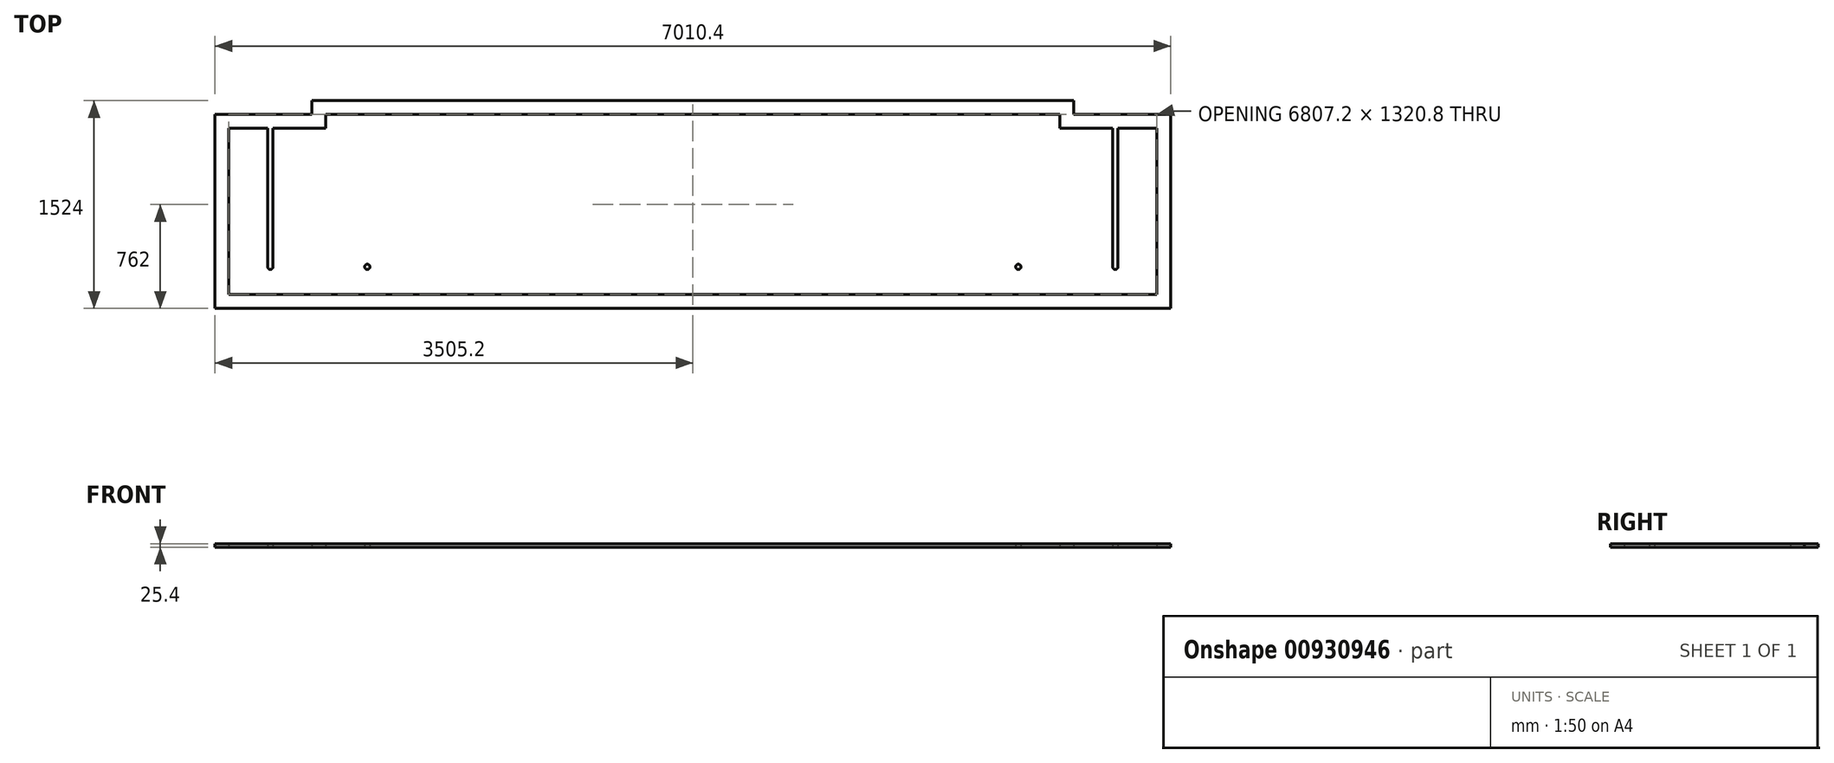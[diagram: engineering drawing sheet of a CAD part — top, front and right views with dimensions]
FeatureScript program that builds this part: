
annotation { "Feature Type Name" : "Feature", "Feature Type Description" : "" }
export const myFeature = defineFeature(function(context is Context, id is Id, definition is map)
    precondition{}
    {
        {
            var Q0;
            Q0=qCreatedBy(makeId("Top.planeOp"),FACE);
            var sketch = newSketch(context, id + "F0", { "sketchPlane" : qUnion([Q0])});
            skLineSegment(sketch, "E0.top", {"start": v(0, -1422.4) * mm, "end": v(7010.4, -1422.4) * mm});
            skLineSegment(sketch, "E0.left", {"start": v(0, 0) * mm, "end": v(0, -1422.4) * mm});
            skLineSegment(sketch, "E0.right", {"start": v(7010.4, 0) * mm, "end": v(7010.4, -1422.4) * mm});
            skLineSegment(sketch, "E1.top", {"start": v(101.6, -1320.8) * mm, "end": v(6908.8, -1320.8) * mm});
            skLineSegment(sketch, "E1.left", {"start": v(101.6, -101.6) * mm, "end": v(101.6, -1320.8) * mm});
            skLineSegment(sketch, "E1.right", {"start": v(6908.8, -101.6) * mm, "end": v(6908.8, -1320.8) * mm});
            skLineSegment(sketch, "E2.bottom", {"start": v(387.35, -101.6) * mm, "end": v(425.45, -101.6) * mm});
            skLineSegment(sketch, "E2.top", {"start": v(387.35, -1117.6) * mm, "end": v(425.45, -1117.6) * mm});
            skLineSegment(sketch, "E2.left", {"start": v(387.35, -101.6) * mm, "end": v(387.35, -1117.6) * mm});
            skLineSegment(sketch, "E2.right", {"start": v(425.45, -101.6) * mm, "end": v(425.45, -1117.6) * mm});
            skLineSegment(sketch, "E3.bottom", {"start": v(6584.95, -101.6) * mm, "end": v(6623.05, -101.6) * mm});
            skLineSegment(sketch, "E3.top", {"start": v(6584.95, -1117.6) * mm, "end": v(6623.05, -1117.6) * mm});
            skLineSegment(sketch, "E3.left", {"start": v(6584.95, -101.6) * mm, "end": v(6584.95, -1117.6) * mm});
            skLineSegment(sketch, "E3.right", {"start": v(6623.05, -101.6) * mm, "end": v(6623.05, -1117.6) * mm});
            skCircle(sketch, "E4", {"center": v(406.4, -1117.6) * mm, "radius": 19.05 * mm});
            skCircle(sketch, "E5", {"center": v(6604, -1117.6) * mm, "radius": 19.05 * mm});
            skLineSegment(sketch, "E6", {"start": v(101.6, -101.6) * mm, "end": v(812.8, -101.6) * mm});
            skLineSegment(sketch, "E7", {"start": v(812.8, -101.6) * mm, "end": v(812.8, 0) * mm});
            skLineSegment(sketch, "E8", {"start": v(812.8, 0) * mm, "end": v(6197.6, 0) * mm});
            skLineSegment(sketch, "E9", {"start": v(6197.6, 0) * mm, "end": v(6197.6, -101.6) * mm});
            skLineSegment(sketch, "E10", {"start": v(6197.6, -101.6) * mm, "end": v(6908.8, -101.6) * mm});
            skLineSegment(sketch, "E11", {"start": v(0, 0) * mm, "end": v(711.2, 0) * mm});
            skLineSegment(sketch, "E12", {"start": v(711.2, 0) * mm, "end": v(711.2, 101.6) * mm});
            skLineSegment(sketch, "E13", {"start": v(711.2, 101.6) * mm, "end": v(6299.2, 101.6) * mm});
            skLineSegment(sketch, "E14", {"start": v(6299.2, 101.6) * mm, "end": v(6299.2, 0) * mm});
            skLineSegment(sketch, "E15", {"start": v(6299.2, 0) * mm, "end": v(7010.4, 0) * mm});
            skLineSegment(sketch, "E16.bottom", {"start": v(1098.55, 0) * mm, "end": v(1136.65, 0) * mm});
            skLineSegment(sketch, "E16.top", {"start": v(1098.55, -1117.6) * mm, "end": v(1136.65, -1117.6) * mm});
            skLineSegment(sketch, "E16.left", {"start": v(1098.55, 0) * mm, "end": v(1098.55, -1117.6) * mm});
            skLineSegment(sketch, "E16.right", {"start": v(1136.65, 0) * mm, "end": v(1136.65, -1117.6) * mm});
            skLineSegment(sketch, "E17.bottom", {"start": v(5873.75, 0) * mm, "end": v(5911.85, 0) * mm});
            skLineSegment(sketch, "E17.top", {"start": v(5873.75, -1117.6) * mm, "end": v(5911.85, -1117.6) * mm});
            skLineSegment(sketch, "E17.left", {"start": v(5873.75, 0) * mm, "end": v(5873.75, -1117.6) * mm});
            skLineSegment(sketch, "E17.right", {"start": v(5911.85, 0) * mm, "end": v(5911.85, -1117.6) * mm});
            skCircle(sketch, "E18", {"center": v(1117.6, -1117.6) * mm, "radius": 19.05 * mm});
            skCircle(sketch, "E19", {"center": v(5892.8, -1117.6) * mm, "radius": 19.05 * mm});
            skSolve(sketch);
        }
        {
            var Q0;
            Q0=makeQuery(id+"F0.imprint","IMPRINT",FACE,{"disambiguationData":[TD([[makeQuery(id+"F0.imprint","IMPRINT",EDGE,{"derivedFrom":sQuery(id+"F0.wireOp",EDGE,"E0.top")}),1.0]])]});
            var Q1;
            {var subQ0=sQuery(id+"F0.wireOp",EDGE,"E2.left");Q1=makeQuery(id+"F0.imprint","IMPRINT",FACE,{"disambiguationData":[TD([[makeQuery(id+"F0.imprint","IMPRINT",EDGE,{"derivedFrom":subQ0}),1.0]])]});}
            var Q2;
            {var subQ0=sQuery(id+"F0.wireOp",EDGE,"E2.top");Q2=makeQuery(id+"F0.imprint","IMPRINT",FACE,{"disambiguationData":[TD([[makeQuery(id+"F0.imprint","IMPRINT",EDGE,{"derivedFrom":subQ0}),1.0]])]});}
            var Q3;
            {var subQ0=sQuery(id+"F0.wireOp",EDGE,"E2.top");Q3=makeQuery(id+"F0.imprint","IMPRINT",FACE,{"disambiguationData":[TD([[makeQuery(id+"F0.imprint","IMPRINT",EDGE,{"derivedFrom":subQ0}),-1.0]])]});}
            var Q4;
            Q4=makeQuery(id+"F0.imprint","IMPRINT",FACE,{"disambiguationData":[TD([[makeQuery(id+"F0.imprint","IMPRINT",EDGE,{"derivedFrom":sQuery(id+"F0.wireOp",EDGE,"E16.bottom")}),-1.0]])]});
            var Q5;
            {var subQ0=sQuery(id+"F0.wireOp",EDGE,"E16.top");Q5=makeQuery(id+"F0.imprint","IMPRINT",FACE,{"disambiguationData":[TD([[makeQuery(id+"F0.imprint","IMPRINT",EDGE,{"derivedFrom":subQ0}),1.0]])]});}
            var Q6;
            {var subQ0=sQuery(id+"F0.wireOp",EDGE,"E16.top");Q6=makeQuery(id+"F0.imprint","IMPRINT",FACE,{"disambiguationData":[TD([[makeQuery(id+"F0.imprint","IMPRINT",EDGE,{"derivedFrom":subQ0}),-1.0]])]});}
            var Q7;
            Q7=makeQuery(id+"F0.imprint","IMPRINT",FACE,{"disambiguationData":[TD([[makeQuery(id+"F0.imprint","IMPRINT",EDGE,{"derivedFrom":sQuery(id+"F0.wireOp",EDGE,"E17.bottom")}),-1.0]])]});
            var Q8;
            {var subQ0=sQuery(id+"F0.wireOp",EDGE,"E17.top");Q8=makeQuery(id+"F0.imprint","IMPRINT",FACE,{"disambiguationData":[TD([[makeQuery(id+"F0.imprint","IMPRINT",EDGE,{"derivedFrom":subQ0}),1.0]])]});}
            var Q9;
            {var subQ0=sQuery(id+"F0.wireOp",EDGE,"E17.top");Q9=makeQuery(id+"F0.imprint","IMPRINT",FACE,{"disambiguationData":[TD([[makeQuery(id+"F0.imprint","IMPRINT",EDGE,{"derivedFrom":subQ0}),-1.0]])]});}
            var Q10;
            {var subQ0=sQuery(id+"F0.wireOp",EDGE,"E3.left");Q10=makeQuery(id+"F0.imprint","IMPRINT",FACE,{"disambiguationData":[TD([[makeQuery(id+"F0.imprint","IMPRINT",EDGE,{"derivedFrom":subQ0}),1.0]])]});}
            var Q11;
            {var subQ0=sQuery(id+"F0.wireOp",EDGE,"E3.top");Q11=makeQuery(id+"F0.imprint","IMPRINT",FACE,{"disambiguationData":[TD([[makeQuery(id+"F0.imprint","IMPRINT",EDGE,{"derivedFrom":subQ0}),1.0]])]});}
            var Q12;
            {var subQ0=sQuery(id+"F0.wireOp",EDGE,"E3.top");Q12=makeQuery(id+"F0.imprint","IMPRINT",FACE,{"disambiguationData":[TD([[makeQuery(id+"F0.imprint","IMPRINT",EDGE,{"derivedFrom":subQ0}),-1.0]])]});}
            extrude(context, id + "F1", {"entities" : qUnion([Q0, Q1, Q2, Q3, Q4, Q5, Q6, Q7, Q8, Q9, Q10, Q11, Q12]), "depth" : 25.4 * mm, "offsetDistance" : 25.4 * mm});
        }
    });
